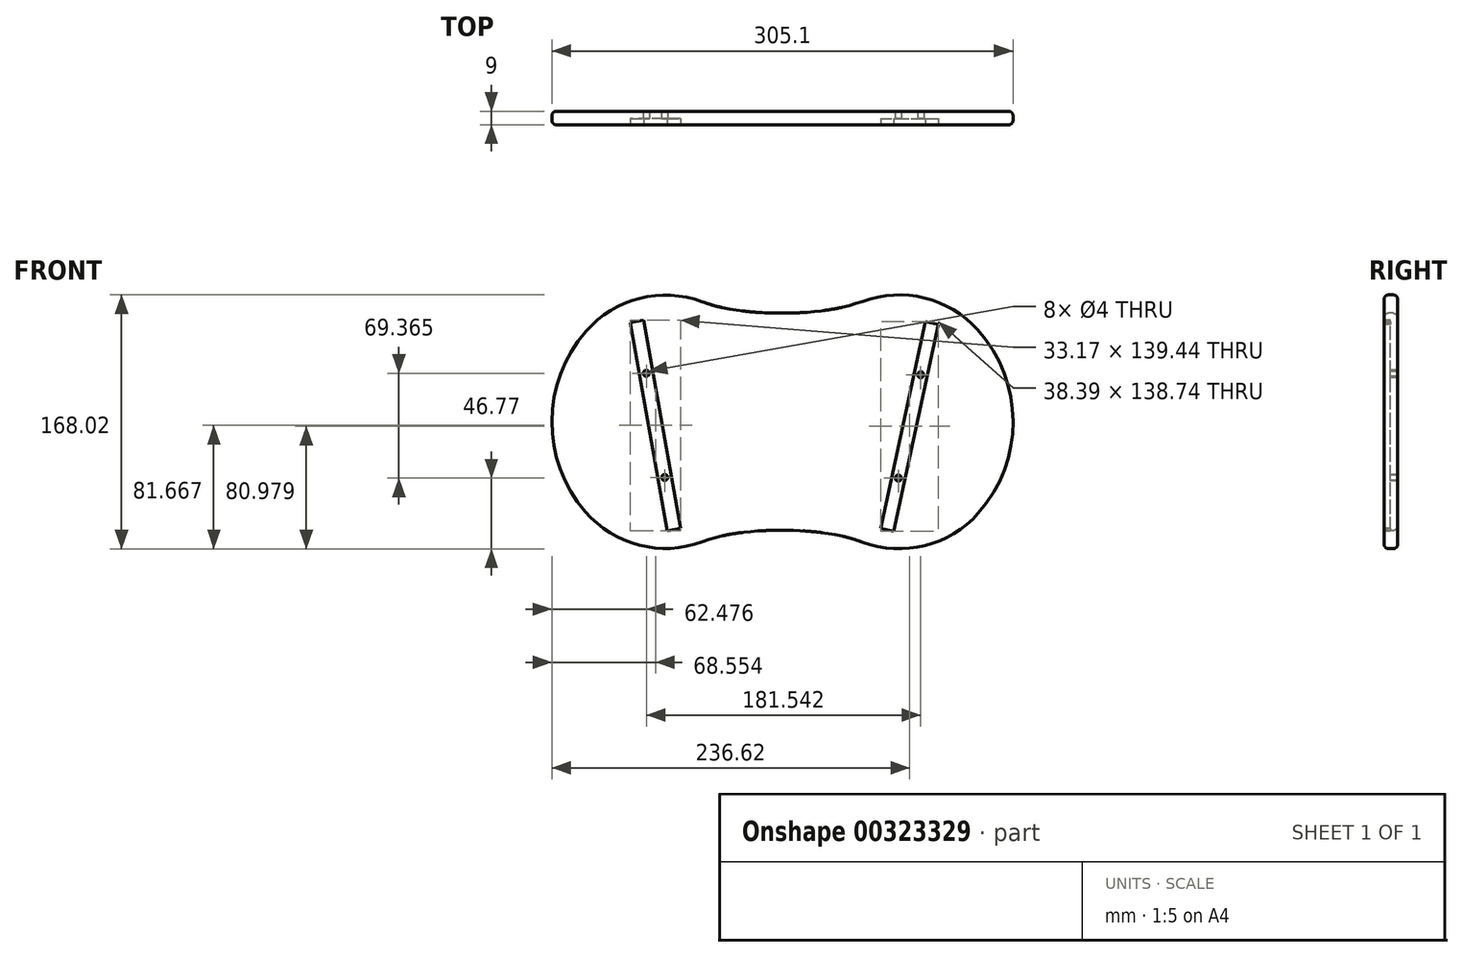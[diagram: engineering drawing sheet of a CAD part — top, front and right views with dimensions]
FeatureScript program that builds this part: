
annotation { "Feature Type Name" : "Feature", "Feature Type Description" : "" }
export const myFeature = defineFeature(function(context is Context, id is Id, definition is map)
    precondition{}
    {
        {
            var Q0;
            Q0=qCreatedBy(makeId("Front.planeOp"),FACE);
            var sketch = newSketch(context, id + "F0", { "sketchPlane" : qUnion([Q0])});
            skPoint(sketch, "E0.middle", {"position": v(0, 0) * mm});
            skPoint(sketch, "E1", {"position": v(-75, 90) * mm});
            skPoint(sketch, "E2", {"position": v(-75, -90) * mm});
            skArc(sketch, "E3", {"start": v(-129.93, 60.04) * mm, "mid": v(-152.55, 0.36) * mm, "end": v(-130.41, -59.49) * mm});
            skPoint(sketch, "E4", {"position": v(75, 90) * mm});
            skPoint(sketch, "E5", {"position": v(75, -90) * mm});
            skArc(sketch, "E6", {"start": v(129.58, -60.44) * mm, "mid": v(152.55, 0.36) * mm, "end": v(129.1, 60.97) * mm});
            skPoint(sketch, "E7", {"position": v(-38.49, 75.36) * mm});
            skPoint(sketch, "E8", {"position": v(37.29, 75.36) * mm});
            skPoint(sketch, "E9", {"position": v(37.29, -75.13) * mm});
            skPoint(sketch, "E10", {"position": v(-38.49, -75.13) * mm});
            skFitSpline(sketch, "E11", {"points": [v(-75, 90) * mm, v(-38.49, 75.36) * mm, v(37.29, 75.36) * mm, v(75, 90) * mm], "startDerivative": vector(106.24, -57.96) * mm, "endDerivative": vector(108.74, 57.11) * mm});
            skArc(sketch, "E12.filletArc", {"start": v(-53.15, 79.55) * mm, "mid": v(-94.57, 81.7) * mm, "end": v(-129.93, 60.04) * mm});
            skFitSpline(sketch, "E13", {"points": [v(-75, -90) * mm, v(-38.49, -75.13) * mm, v(37.29, -75.13) * mm, v(75, -90) * mm], "startDerivative": vector(106.13, 58.85) * mm, "endDerivative": vector(108.63, -58) * mm});
            skArc(sketch, "E14.filletArc", {"start": v(129.1, 60.97) * mm, "mid": v(94, 82) * mm, "end": v(53.13, 79.82) * mm});
            skArc(sketch, "E15.filletArc", {"start": v(53, -79.61) * mm, "mid": v(94.25, -81.85) * mm, "end": v(129.58, -60.44) * mm});
            skArc(sketch, "E16.filletArc", {"start": v(-130.41, -59.49) * mm, "mid": v(-94.83, -81.53) * mm, "end": v(-53.02, -79.33) * mm});
            skSolve(sketch);
        }
        {
            var Q0;
            Q0=makeQuery(id+"F0.imprint","IMPRINT",FACE,{"disambiguationData":[TD([[makeQuery(id+"F0.imprint","IMPRINT",EDGE,{"derivedFrom":sQuery(id+"F0.wireOp",EDGE,"E3")}),1.0]])]});
            extrude(context, id + "F1", {"entities" : qUnion([Q0]), "depth" : 9 * mm});
        }
        {
            var Q0;
            Q0=makeQuery(id+"F1.opExtrude","CAP_FACE",FACE,{"disambiguationData":[OSD([sQuery(id+"F0.wireOp",EDGE,"E3"),sQuery(id+"F0.wireOp",EDGE,"E6"),sQuery(id+"F0.wireOp",EDGE,"E11"),sQuery(id+"F0.wireOp",EDGE,"E12.filletArc"),sQuery(id+"F0.wireOp",EDGE,"E13"),sQuery(id+"F0.wireOp",EDGE,"E14.filletArc"),sQuery(id+"F0.wireOp",EDGE,"E15.filletArc"),sQuery(id+"F0.wireOp",EDGE,"E16.filletArc")])],"isStart":false});
            var sketch = newSketch(context, id + "F2", { "sketchPlane" : qUnion([Q0])});
            skLineSegment(sketch, "E17", {"start": v(0, -65.2) * mm, "end": v(0, 59.35) * mm});
            skLineSegment(sketch, "E18", {"start": v(-67.4, -70.44) * mm, "end": v(-91.72, 67.43) * mm});
            skLineSegment(sketch, "E19", {"start": v(64.87, -70.44) * mm, "end": v(94.47, 66.4) * mm});
            skLineSegment(sketch, "E20.0", {"start": v(-76.27, -72) * mm, "end": v(-100.58, 65.87) * mm});
            skLineSegment(sketch, "E21.0", {"start": v(73.67, -72.34) * mm, "end": v(103.26, 64.5) * mm});
            skLineSegment(sketch, "E22", {"start": v(-100.58, 65.87) * mm, "end": v(-91.72, 67.43) * mm});
            skLineSegment(sketch, "E23", {"start": v(-76.27, -72) * mm, "end": v(-67.4, -70.44) * mm});
            skLineSegment(sketch, "E24", {"start": v(64.87, -70.44) * mm, "end": v(73.67, -72.34) * mm});
            skLineSegment(sketch, "E25", {"start": v(94.47, 66.4) * mm, "end": v(103.26, 64.5) * mm});
            skSolve(sketch);
        }
        {
            var Q0;
            Q0=makeQuery(id+"F1.opExtrude","CAP_EDGE",EDGE,{"disambiguationData":[OSD([sQuery(id+"F0.wireOp",EDGE,"E12.filletArc")])],"isStart":false});
            var Q1;
            Q1=makeQuery(id+"F1.opExtrude","CAP_EDGE",EDGE,{"disambiguationData":[OSD([sQuery(id+"F0.wireOp",EDGE,"E11")])],"isStart":false});
            var Q2;
            Q2=makeQuery(id+"F1.opExtrude","CAP_EDGE",EDGE,{"disambiguationData":[OSD([sQuery(id+"F0.wireOp",EDGE,"E14.filletArc")])],"isStart":false});
            var Q3;
            Q3=makeQuery(id+"F1.opExtrude","CAP_EDGE",EDGE,{"disambiguationData":[OSD([sQuery(id+"F0.wireOp",EDGE,"E6")])],"isStart":false});
            var Q4;
            Q4=makeQuery(id+"F1.opExtrude","CAP_EDGE",EDGE,{"disambiguationData":[OSD([sQuery(id+"F0.wireOp",EDGE,"E15.filletArc")])],"isStart":false});
            var Q5;
            Q5=makeQuery(id+"F1.opExtrude","CAP_EDGE",EDGE,{"disambiguationData":[OSD([sQuery(id+"F0.wireOp",EDGE,"E13")])],"isStart":false});
            var Q6;
            Q6=makeQuery(id+"F1.opExtrude","CAP_EDGE",EDGE,{"disambiguationData":[OSD([sQuery(id+"F0.wireOp",EDGE,"E16.filletArc")])],"isStart":false});
            var Q7;
            Q7=makeQuery(id+"F1.opExtrude","CAP_EDGE",EDGE,{"disambiguationData":[OSD([sQuery(id+"F0.wireOp",EDGE,"E3")])],"isStart":false});
            var Q8;
            Q8=makeQuery(id+"F1.opExtrude","CAP_EDGE",EDGE,{"disambiguationData":[OSD([sQuery(id+"F0.wireOp",EDGE,"E12.filletArc")])],"isStart":true});
            fillet(context, id + "F3", {"entities" : qUnion([Q0, Q1, Q2, Q3, Q4, Q5, Q6, Q7, Q8]), "radius" : 3 * mm, "tangentPropagation" : true, "allowEdgeOverflow" : false});
        }
        {
            var Q0;
            Q0=makeQuery(id+"F2.imprint","IMPRINT",FACE,{"disambiguationData":[TD([[makeQuery(id+"F2.imprint","IMPRINT",EDGE,{"derivedFrom":sQuery(id+"F2.wireOp",EDGE,"E19")}),-1.0]])]});
            var Q1;
            Q1=makeQuery(id+"F2.imprint","IMPRINT",FACE,{"disambiguationData":[TD([[makeQuery(id+"F2.imprint","IMPRINT",EDGE,{"derivedFrom":sQuery(id+"F2.wireOp",EDGE,"E18")}),1.0]])]});
            extrude(context, id + "F4", {"entities" : qUnion([Q0, Q1]), "operationType" : NewBodyOperationType.REMOVE, "oppositeDirection" : true, "depth" : 4 * mm});
        }
        {
            var Q0;
            Q0=makeQuery(id+"F1.opExtrude","CAP_FACE",FACE,{"disambiguationData":[OSD([sQuery(id+"F0.wireOp",EDGE,"E3"),sQuery(id+"F0.wireOp",EDGE,"E6"),sQuery(id+"F0.wireOp",EDGE,"E11"),sQuery(id+"F0.wireOp",EDGE,"E12.filletArc"),sQuery(id+"F0.wireOp",EDGE,"E13"),sQuery(id+"F0.wireOp",EDGE,"E14.filletArc"),sQuery(id+"F0.wireOp",EDGE,"E15.filletArc"),sQuery(id+"F0.wireOp",EDGE,"E16.filletArc")])],"isStart":false});
            var sketch = newSketch(context, id + "F5", { "sketchPlane" : qUnion([Q0])});
            skLineSegment(sketch, "E26", {"start": v(-96.15, 66.65) * mm, "end": v(-71.84, -71.22) * mm});
            skLineSegment(sketch, "E27", {"start": v(69.27, -71.39) * mm, "end": v(98.87, 65.45) * mm});
            skPoint(sketch, "E28", {"position": v(91.47, 31.24) * mm});
            skPoint(sketch, "E29", {"position": v(76.67, -37.18) * mm});
            skPoint(sketch, "E30", {"position": v(-77.92, -36.75) * mm});
            skPoint(sketch, "E31", {"position": v(-90.07, 32.19) * mm});
            skSolve(sketch);
        }
        {
            var Q0;
            Q0=sQuery(id+"F5.wireOp",VERTEX,"E31");
            var Q1;
            Q1=sQuery(id+"F5.wireOp",VERTEX,"E30");
            var Q2;
            Q2=sQuery(id+"F5.wireOp",VERTEX,"E29");
            var Q3;
            Q3=sQuery(id+"F5.wireOp",VERTEX,"E28");
            var Q4;
            Q4=makeQuery(id+"F1.opExtrude","SWEPT_BODY",BODY,{"disambiguationData":[OSD([sQuery(id+"F0.wireOp",EDGE,"E3"),sQuery(id+"F0.wireOp",EDGE,"E6"),sQuery(id+"F0.wireOp",EDGE,"E11"),sQuery(id+"F0.wireOp",EDGE,"E12.filletArc"),sQuery(id+"F0.wireOp",EDGE,"E13"),sQuery(id+"F0.wireOp",EDGE,"E14.filletArc"),sQuery(id+"F0.wireOp",EDGE,"E15.filletArc"),sQuery(id+"F0.wireOp",EDGE,"E16.filletArc")])]});
            hole(context, id + "F6", {"style" : HoleStyle.SIMPLE, "endStyle" : HoleEndStyle.THROUGH, "holeDiameter" : 4 * mm, "tappedDepth" : 12 * mm, "tapClearance" : 3, "locations" : qUnion([Q0, Q1, Q2, Q3]), "scope" : qUnion([Q4])});
        }
    });
